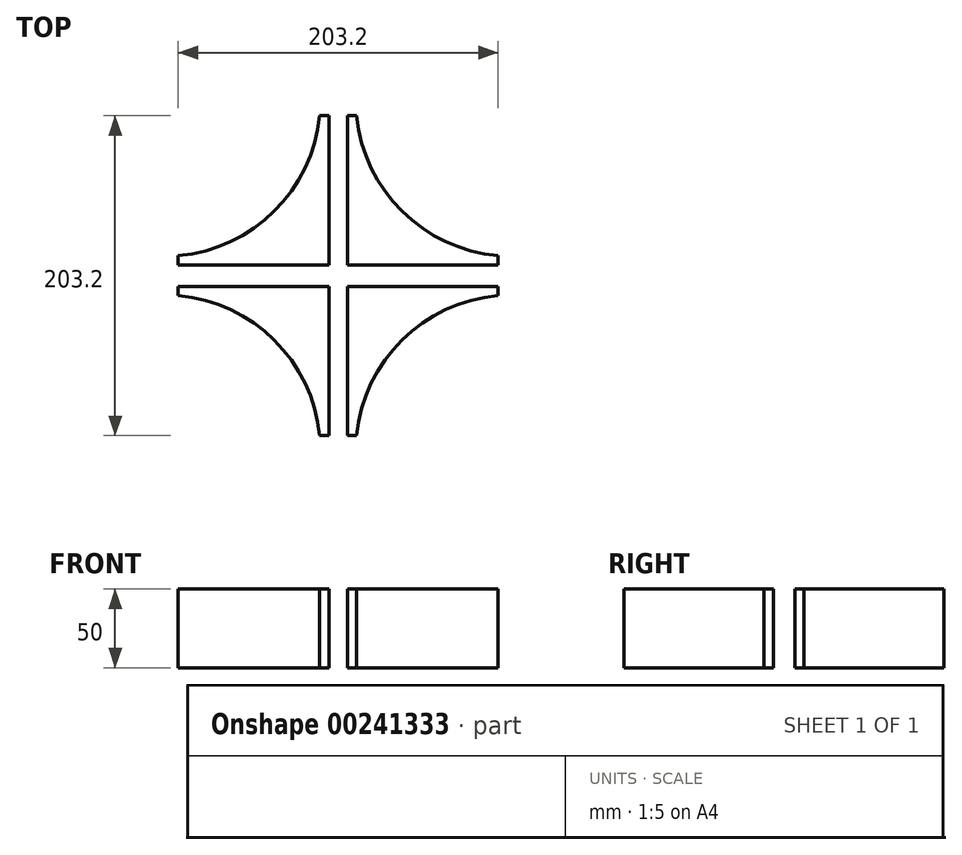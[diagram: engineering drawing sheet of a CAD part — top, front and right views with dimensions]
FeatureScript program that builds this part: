
annotation { "Feature Type Name" : "Feature", "Feature Type Description" : "" }
export const myFeature = defineFeature(function(context is Context, id is Id, definition is map)
    precondition{}
    {
        {
            var Q0;
            Q0=qCreatedBy(makeId("Top.planeOp"),FACE);
            var sketch = newSketch(context, id + "F0", { "sketchPlane" : qUnion([Q0])});
            skLineSegment(sketch, "E0", {"start": v(-5.84, -6.88) * mm, "end": v(-5.84, -101.6) * mm});
            skLineSegment(sketch, "E1", {"start": v(-5.84, -6.88) * mm, "end": v(-101.6, -6.88) * mm});
            skPoint(sketch, "E2.end.orphan", {"position": v(-5.84, 0) * mm});
            skPoint(sketch, "E2.start.orphan", {"position": v(0, 0) * mm});
            skLineSegment(sketch, "E3", {"start": v(-101.6, -6.88) * mm, "end": v(-101.6, -12.72) * mm});
            skLineSegment(sketch, "E4", {"start": v(-5.84, -101.6) * mm, "end": v(-11.68, -101.6) * mm});
            skLineSegment(sketch, "E5", {"start": v(-5.84, -6.88) * mm, "end": v(-91.79, -92.08) * mm, "construction": true});
            skArc(sketch, "E6", {"start": v(-11.68, -101.6) * mm, "mid": v(-40.59, -40.92) * mm, "end": v(-101.6, -12.72) * mm});
            skLineSegment(sketch, "E7.MirrorCS", {"start": v(5.84, -6.88) * mm, "end": v(101.6, -6.88) * mm});
            skLineSegment(sketch, "E8.MirrorCS", {"start": v(101.6, -6.88) * mm, "end": v(101.6, -12.72) * mm});
            skArc(sketch, "E9.MirrorCS", {"start": v(11.68, -101.6) * mm, "mid": v(40.59, -40.92) * mm, "end": v(101.6, -12.72) * mm});
            skLineSegment(sketch, "E10.MirrorCS", {"start": v(5.84, -6.88) * mm, "end": v(5.84, -101.6) * mm});
            skLineSegment(sketch, "E11.MirrorCS", {"start": v(5.84, -101.6) * mm, "end": v(11.68, -101.6) * mm});
            skLineSegment(sketch, "E12", {"start": v(0, 0) * mm, "end": v(-5.84, 0) * mm, "construction": true});
            skLineSegment(sketch, "E13.MirrorCS", {"start": v(-5.84, 6.88) * mm, "end": v(-101.6, 6.88) * mm});
            skArc(sketch, "E14.MirrorCS", {"start": v(-11.68, 101.6) * mm, "mid": v(-40.59, 40.92) * mm, "end": v(-101.6, 12.72) * mm});
            skLineSegment(sketch, "E15.MirrorCS", {"start": v(-5.84, 6.88) * mm, "end": v(-5.84, 101.6) * mm});
            skLineSegment(sketch, "E16.MirrorCS", {"start": v(-101.6, 6.88) * mm, "end": v(-101.6, 12.72) * mm});
            skLineSegment(sketch, "E17.MirrorCS", {"start": v(-5.84, 101.6) * mm, "end": v(-11.68, 101.6) * mm});
            skLineSegment(sketch, "E18.MirrorCS", {"start": v(5.84, 6.88) * mm, "end": v(5.84, 101.6) * mm});
            skLineSegment(sketch, "E19.MirrorCS", {"start": v(5.84, 6.88) * mm, "end": v(101.6, 6.88) * mm});
            skArc(sketch, "E20.MirrorCS", {"start": v(11.68, 101.6) * mm, "mid": v(40.59, 40.92) * mm, "end": v(101.6, 12.72) * mm});
            skLineSegment(sketch, "E21.MirrorCS", {"start": v(101.6, 6.88) * mm, "end": v(101.6, 12.72) * mm});
            skLineSegment(sketch, "E22.MirrorCS", {"start": v(5.84, 101.6) * mm, "end": v(11.68, 101.6) * mm});
            skSolve(sketch);
        }
        {
            var Q0;
            Q0=makeQuery(id+"F0.imprint","IMPRINT",FACE,{"disambiguationData":[TD([[makeQuery(id+"F0.imprint","IMPRINT",EDGE,{"derivedFrom":sQuery(id+"F0.wireOp",EDGE,"E0")}),-1.0]])]});
            var Q1;
            Q1=makeQuery(id+"F0.imprint","IMPRINT",FACE,{"disambiguationData":[TD([[makeQuery(id+"F0.imprint","IMPRINT",EDGE,{"derivedFrom":sQuery(id+"F0.wireOp",EDGE,"E13.MirrorCS")}),-1.0]])]});
            var Q2;
            Q2=makeQuery(id+"F0.imprint","IMPRINT",FACE,{"disambiguationData":[TD([[makeQuery(id+"F0.imprint","IMPRINT",EDGE,{"derivedFrom":sQuery(id+"F0.wireOp",EDGE,"E19.MirrorCS")}),1.0]])]});
            var Q3;
            Q3=makeQuery(id+"F0.imprint","IMPRINT",FACE,{"disambiguationData":[TD([[makeQuery(id+"F0.imprint","IMPRINT",EDGE,{"derivedFrom":sQuery(id+"F0.wireOp",EDGE,"E7.MirrorCS")}),-1.0]])]});
            extrude(context, id + "F1", {"entities" : qUnion([Q0, Q1, Q2, Q3]), "depth" : 50 * mm});
        }
    });
